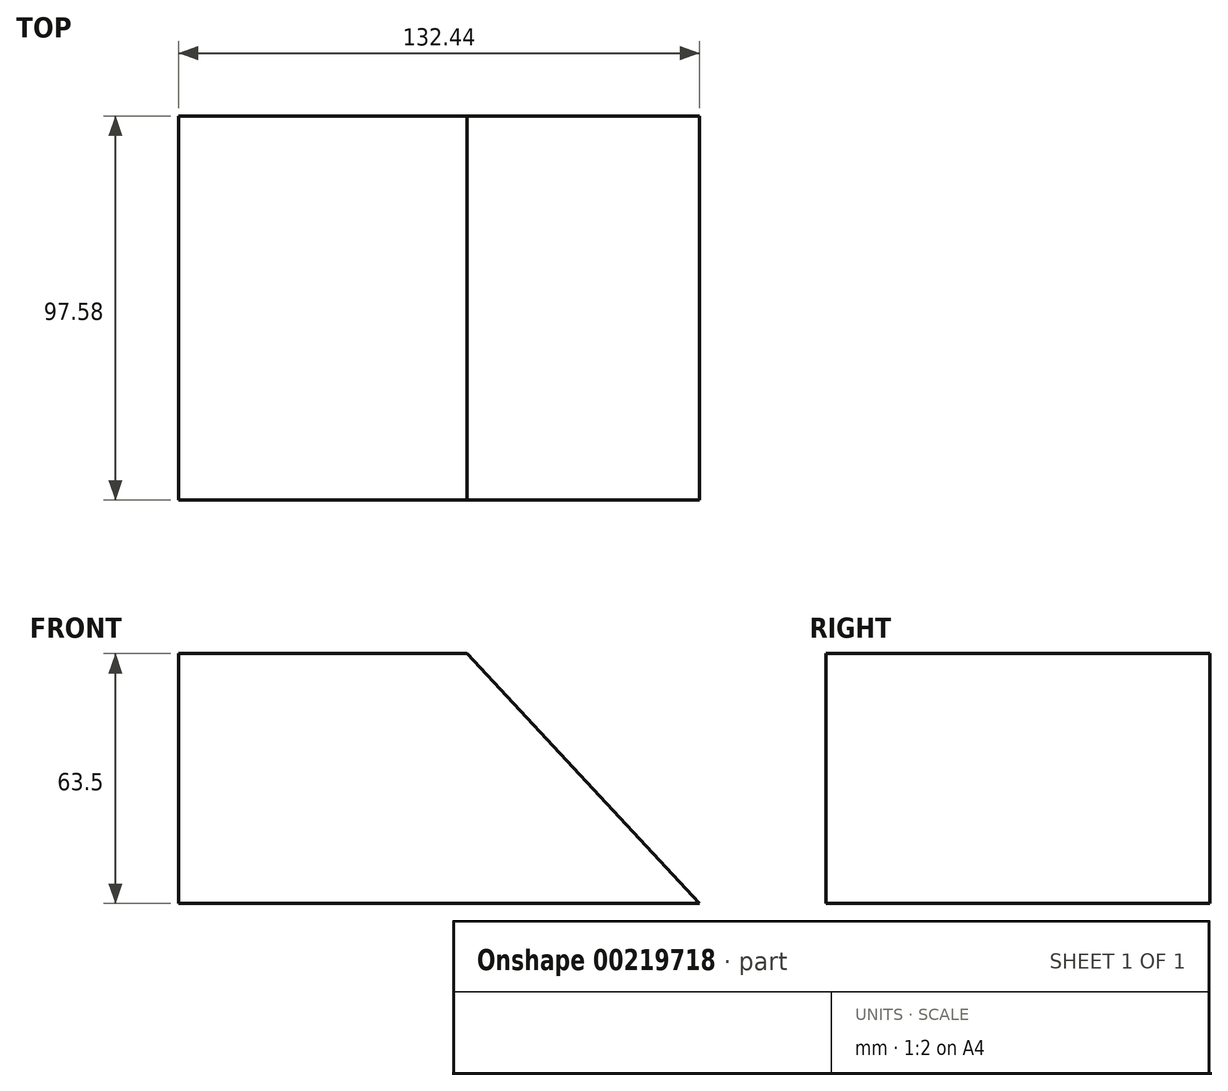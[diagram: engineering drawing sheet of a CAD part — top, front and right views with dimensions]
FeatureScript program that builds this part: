
annotation { "Feature Type Name" : "Feature", "Feature Type Description" : "" }
export const myFeature = defineFeature(function(context is Context, id is Id, definition is map)
    precondition{}
    {
        {
            var Q0;
            Q0=qCreatedBy(makeId("Top.planeOp"),FACE);
            var sketch = newSketch(context, id + "F0", { "sketchPlane" : qUnion([Q0])});
            skLineSegment(sketch, "E0.bottom", {"start": v(-73.38, 48.79) * mm, "end": v(73.38, 48.79) * mm});
            skLineSegment(sketch, "E0.top", {"start": v(-73.38, -48.79) * mm, "end": v(73.38, -48.79) * mm});
            skLineSegment(sketch, "E0.left", {"start": v(-73.38, 48.79) * mm, "end": v(-73.38, -48.79) * mm});
            skLineSegment(sketch, "E0.right", {"start": v(73.38, 48.79) * mm, "end": v(73.38, -48.79) * mm});
            skPoint(sketch, "E0.middle", {"position": v(0, 0) * mm});
            skSolve(sketch);
        }
        {
            var Q0;
            Q0 = qSketchRegion(id + "F0", true);
            extrude(context, id + "F1", {"entities" : qUnion([Q0]), "depth" : 63.5 * mm});
        }
        {
            var Q0;
            Q0=makeQuery(id+"F1.opExtrude","SWEPT_FACE",FACE,{"disambiguationData":[OSD([sQuery(id+"F0.wireOp",EDGE,"E0.top")])]});
            var sketch = newSketch(context, id + "F2", { "sketchPlane" : qUnion([Q0])});
            skLineSegment(sketch, "E1.0", {"start": v(-73.38, 63.5) * mm, "end": v(73.38, 63.5) * mm});
            skLineSegment(sketch, "E2.0", {"start": v(73.38, 63.5) * mm, "end": v(73.38, 0) * mm});
            skLineSegment(sketch, "E3", {"start": v(0, 63.5) * mm, "end": v(73.38, 0) * mm});
            skSolve(sketch);
        }
        {
            var Q0;
            {var subQ0=sQuery(id+"F2.wireOp",EDGE,"E2.0");Q0=makeQuery(id+"F2.imprint","IMPRINT",FACE,{"disambiguationData":[TD([[makeQuery(id+"F2.imprint","IMPRINT",EDGE,{"derivedFrom":subQ0}),-1.0]])]});}
            extrude(context, id + "F3", {"entities" : qUnion([Q0]), "operationType" : NewBodyOperationType.REMOVE, "endBound" : BoundingType.THROUGH_ALL, "oppositeDirection" : true, "depth" : 25.4 * mm});
        }
        {
            var Q0;
            Q0=makeQuery(id+"F1.opExtrude","SWEPT_FACE",FACE,{"disambiguationData":[OSD([sQuery(id+"F0.wireOp",EDGE,"E0.top")])]});
            var sketch = newSketch(context, id + "F4", { "sketchPlane" : qUnion([Q0])});
            skPoint(sketch, "E4.0", {"position": v(0, 63.5) * mm});
            skLineSegment(sketch, "E5.0", {"start": v(-73.38, 0) * mm, "end": v(73.38, 0) * mm});
            skLineSegment(sketch, "E6", {"start": v(0, 63.5) * mm, "end": v(59.06, 0) * mm});
            skSolve(sketch);
        }
        {
            var Q0;
            {var subQ2=sQuery(id+"F4.wireOp",EDGE,"E6");Q0=makeQuery(id+"F4.imprint","IMPRINT",FACE,{"disambiguationData":[TD([[makeQuery(id+"F4.imprint","IMPRINT",EDGE,{"derivedFrom":subQ2}),1.0]])]});}
            extrude(context, id + "F5", {"entities" : qUnion([Q0]), "operationType" : NewBodyOperationType.REMOVE, "endBound" : BoundingType.THROUGH_ALL, "oppositeDirection" : true, "depth" : 25.4 * mm});
        }
    });
